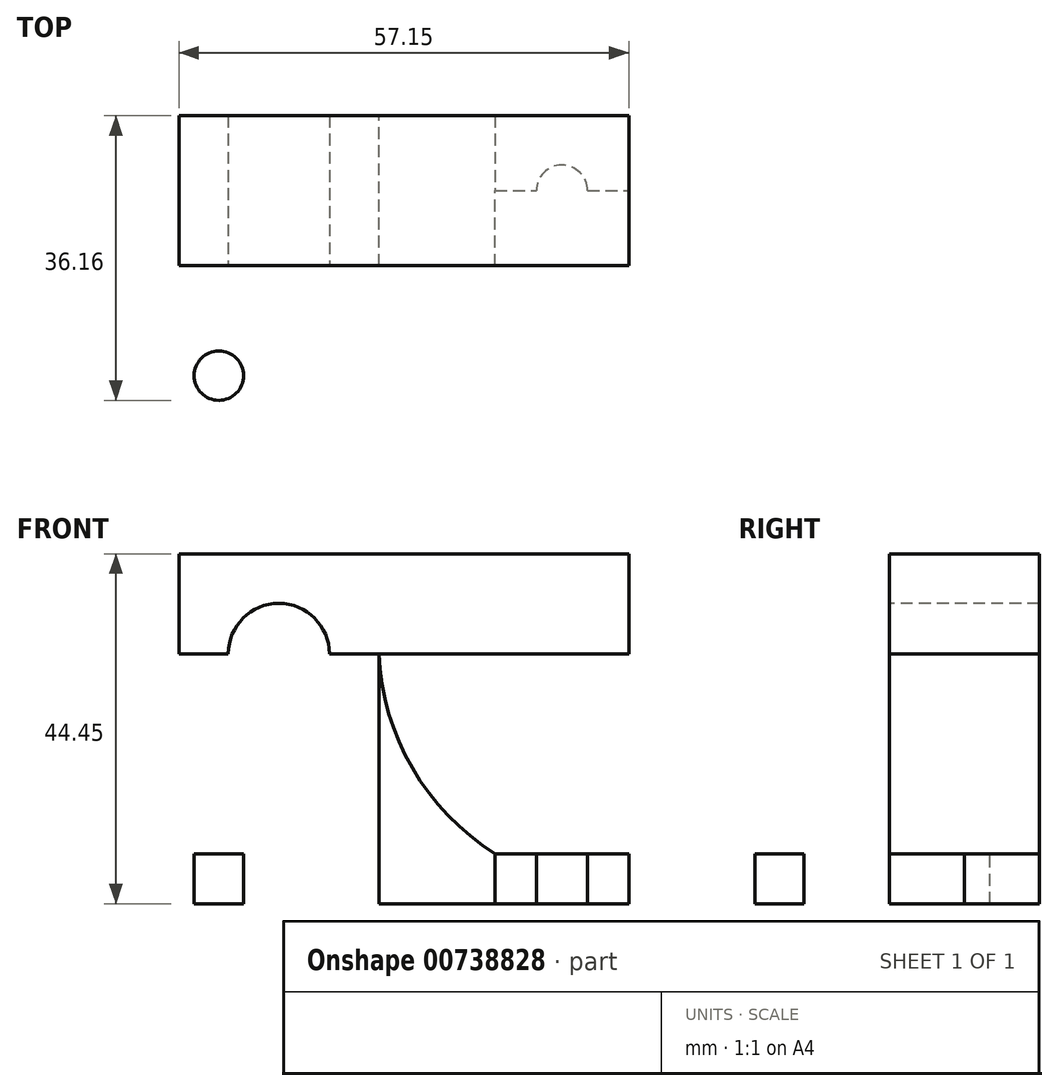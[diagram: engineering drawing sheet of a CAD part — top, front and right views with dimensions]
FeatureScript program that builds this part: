
annotation { "Feature Type Name" : "Feature", "Feature Type Description" : "" }
export const myFeature = defineFeature(function(context is Context, id is Id, definition is map)
    precondition{}
    {
        {
            var Q0;
            Q0=qCreatedBy(makeId("Front.planeOp"),FACE);
            var sketch = newSketch(context, id + "F0", { "sketchPlane" : qUnion([Q0])});
            skLineSegment(sketch, "E0", {"start": v(0, 0) * mm, "end": v(0, 44.45) * mm});
            skLineSegment(sketch, "E1", {"start": v(0, 44.45) * mm, "end": v(57.15, 44.45) * mm});
            skLineSegment(sketch, "E2", {"start": v(57.15, 44.45) * mm, "end": v(57.15, 0) * mm});
            skLineSegment(sketch, "E3", {"start": v(57.15, 0) * mm, "end": v(0, 0) * mm});
            skSolve(sketch);
        }
        {
            var Q0;
            Q0 = qSketchRegion(id + "F0", true);
            extrude(context, id + "F1", {"entities" : qUnion([Q0]), "depth" : 38.1 * mm, "offsetDistance" : 25.4 * mm});
        }
        {
            var Q0;
            Q0=makeQuery(id+"F1.opExtrude","CAP_FACE",FACE,{"disambiguationData":[OSD([sQuery(id+"F0.wireOp",EDGE,"E0"),sQuery(id+"F0.wireOp",EDGE,"E1"),sQuery(id+"F0.wireOp",EDGE,"E2"),sQuery(id+"F0.wireOp",EDGE,"E3")])],"isStart":false});
            var sketch = newSketch(context, id + "F2", { "sketchPlane" : qUnion([Q0])});
            skLineSegment(sketch, "E4", {"start": v(0, 6.35) * mm, "end": v(57.15, 6.35) * mm});
            skSolve(sketch);
        }
        {
            var Q0;
            {var subQ0=sQuery(id+"F2.wireOp",EDGE,"E4");Q0=makeQuery(id+"F2.imprint","IMPRINT",FACE,{"disambiguationData":[TD([[makeQuery(id+"F2.imprint","IMPRINT",EDGE,{"derivedFrom":subQ0}),1.0]])]});}
            extrude(context, id + "F3", {"entities" : qUnion([Q0]), "operationType" : NewBodyOperationType.REMOVE, "oppositeDirection" : true, "depth" : 19.05 * mm, "offsetDistance" : 25.4 * mm});
        }
        {
            var Q0;
            Q0=makeQuery(id+"F1.opExtrude","CAP_EDGE",EDGE,{"disambiguationData":[OSD([sQuery(id+"F0.wireOp",EDGE,"E0")])],"isStart":false});
            var Q1;
            Q1=makeQuery(id+"F1.opExtrude","CAP_EDGE",EDGE,{"disambiguationData":[OSD([sQuery(id+"F0.wireOp",EDGE,"E2")])],"isStart":false});
            fillet(context, id + "F4", {"entities" : qUnion([Q0, Q1]), "radius" : 5.08 * mm, "tangentPropagation" : true, "allowEdgeOverflow" : false});
        }
        {
            var Q0;
            Q0=makeQuery(id+"F3.boolean.opBoolean","COPY",FACE,{"derivedFrom":makeQuery(id+"F3.opExtrude","CAP_FACE",FACE,{"disambiguationData":[OSD([sQuery(id+"F0.wireOp",EDGE,"E0"),sQuery(id+"F0.wireOp",EDGE,"E1"),sQuery(id+"F0.wireOp",EDGE,"E2"),sQuery(id+"F2.wireOp",EDGE,"E4")])],"isStart":false})});
            var sketch = newSketch(context, id + "F5", { "sketchPlane" : qUnion([Q0])});
            skLineSegment(sketch, "E5", {"start": v(12.7, 44.45) * mm, "end": v(12.7, 6.35) * mm});
            skLineSegment(sketch, "E6", {"start": v(0, 31.75) * mm, "end": v(57.15, 31.75) * mm});
            skCircle(sketch, "E7", {"center": v(12.7, 31.75) * mm, "radius": 6.42 * mm});
            skLineSegment(sketch, "E8", {"start": v(25.4, 44.45) * mm, "end": v(25.4, 6.35) * mm});
            skPoint(sketch, "E8.endSnap0", {"position": v(28.58, 6.35) * mm});
            skArc(sketch, "E9", {"start": v(25.4, 31.75) * mm, "mid": v(12.7, 43.9) * mm, "end": v(0, 31.75) * mm});
            skArc(sketch, "E10", {"start": v(25.4, 31.75) * mm, "mid": v(29.66, 17.24) * mm, "end": v(40.16, 6.35) * mm});
            skSolve(sketch);
        }
        {
            var Q0;
            {var subQ0=sQuery(id+"F5.wireOp",EDGE,"E7");var subQ1=sQuery(id+"F5.wireOp",EDGE,"E5");var subQ2=makeQuery(id+"F5.imprint","INTERSECT",VERTEX,{"disambiguationData":[OD(0.0)],"derivedFrom":[subQ1,subQ0]});Q0=makeQuery(id+"F5.imprint","IMPRINT",FACE,{"disambiguationData":[TD([[makeQuery(id+"F5.imprint","IMPRINT",EDGE,{"disambiguationData":[TD([[subQ2,-1.0]])],"derivedFrom":subQ1}),-1.0]])]});}
            var Q1;
            {var subQ0=sQuery(id+"F5.wireOp",EDGE,"E7");var subQ1=sQuery(id+"F5.wireOp",EDGE,"E5");var subQ2=makeQuery(id+"F5.imprint","INTERSECT",VERTEX,{"disambiguationData":[OD(0.0)],"derivedFrom":[subQ1,subQ0]});Q1=makeQuery(id+"F5.imprint","IMPRINT",FACE,{"disambiguationData":[TD([[makeQuery(id+"F5.imprint","IMPRINT",EDGE,{"disambiguationData":[TD([[subQ2,-1.0]])],"derivedFrom":subQ1}),1.0]])]});}
            var Q2;
            {var subQ0=sQuery(id+"F5.wireOp",EDGE,"E6");var subQ1=sQuery(id+"F5.wireOp",EDGE,"E5");var subQ2=makeQuery(id+"F5.imprint","INTERSECT",VERTEX,{"derivedFrom":[subQ1,subQ0]});Q2=makeQuery(id+"F5.imprint","IMPRINT",FACE,{"disambiguationData":[TD([[makeQuery(id+"F5.imprint","IMPRINT",EDGE,{"disambiguationData":[TD([[subQ2,-1.0]])],"derivedFrom":subQ1}),-1.0]])]});}
            var Q3;
            {var subQ0=sQuery(id+"F5.wireOp",EDGE,"E6");var subQ1=sQuery(id+"F5.wireOp",EDGE,"E5");var subQ2=makeQuery(id+"F5.imprint","INTERSECT",VERTEX,{"derivedFrom":[subQ1,subQ0]});Q3=makeQuery(id+"F5.imprint","IMPRINT",FACE,{"disambiguationData":[TD([[makeQuery(id+"F5.imprint","IMPRINT",EDGE,{"disambiguationData":[TD([[subQ2,-1.0]])],"derivedFrom":subQ1}),1.0]])]});}
            var Q4;
            {var subQ0=sQuery(id+"F5.wireOp",EDGE,"E5");var subQ1=makeQuery(id+"F3.boolean.opBoolean","COPY",EDGE,{"derivedFrom":makeQuery(id+"F3.opExtrude","CAP_EDGE",EDGE,{"disambiguationData":[OSD([sQuery(id+"F0.wireOp",EDGE,"E1")])],"isStart":false})});var subQ2=makeQuery(id+"F5.imprint","INTERSECT",VERTEX,{"derivedFrom":[subQ1,subQ0]});Q4=makeQuery(id+"F5.imprint","IMPRINT",FACE,{"disambiguationData":[TD([[makeQuery(id+"F5.imprint","IMPRINT",EDGE,{"disambiguationData":[TD([[subQ2,-1.0]])],"derivedFrom":subQ0}),-1.0]])]});}
            var Q5;
            {var subQ0=sQuery(id+"F5.wireOp",EDGE,"E5");var subQ1=makeQuery(id+"F3.boolean.opBoolean","COPY",EDGE,{"derivedFrom":makeQuery(id+"F3.opExtrude","CAP_EDGE",EDGE,{"disambiguationData":[OSD([sQuery(id+"F0.wireOp",EDGE,"E1")])],"isStart":false})});var subQ2=makeQuery(id+"F5.imprint","INTERSECT",VERTEX,{"derivedFrom":[subQ1,subQ0]});Q5=makeQuery(id+"F5.imprint","IMPRINT",FACE,{"disambiguationData":[TD([[makeQuery(id+"F5.imprint","IMPRINT",EDGE,{"disambiguationData":[TD([[subQ2,-1.0]])],"derivedFrom":subQ0}),1.0]])]});}
            var Q6;
            {var subQ3=sQuery(id+"F5.wireOp",EDGE,"E10");Q6=makeQuery(id+"F5.imprint","IMPRINT",FACE,{"disambiguationData":[TD([[makeQuery(id+"F5.imprint","IMPRINT",EDGE,{"derivedFrom":subQ3}),1.0]])]});}
            var Q7;
            {var subQ1=makeQuery(id+"F3.boolean.opBoolean","COPY",EDGE,{"derivedFrom":makeQuery(id+"F3.opExtrude","CAP_EDGE",EDGE,{"disambiguationData":[OSD([sQuery(id+"F0.wireOp",EDGE,"E2")])],"isStart":false})});var subQ5=makeQuery(id+"F3.boolean.opBoolean","COPY",EDGE,{"derivedFrom":makeQuery(id+"F3.opExtrude","CAP_EDGE",EDGE,{"disambiguationData":[OSD([sQuery(id+"F0.wireOp",EDGE,"E1")])],"isStart":false})});var subQ7=makeQuery(id+"F5.imprint","INTERSECT",VERTEX,{"derivedFrom":[subQ5,subQ1]});Q7=makeQuery(id+"F5.imprint","IMPRINT",FACE,{"disambiguationData":[TD([[makeQuery(id+"F5.imprint","IMPRINT",EDGE,{"disambiguationData":[TD([[subQ7,1.0]])],"derivedFrom":subQ5}),-1.0]])]});}
            extrude(context, id + "F6", {"entities" : qUnion([Q0, Q1, Q2, Q3, Q4, Q5, Q6, Q7]), "operationType" : NewBodyOperationType.REMOVE, "endBound" : BoundingType.THROUGH_ALL, "oppositeDirection" : true, "depth" : 25.4 * mm, "offsetDistance" : 25.4 * mm});
        }
        {
            var Q0;
            {var subQ0=sQuery(id+"F2.wireOp",EDGE,"E4");Q0=makeQuery(id+"F6.boolean.opBoolean","MERGE",FACE,{"derivedFrom":[makeQuery(id+"F3.boolean.opBoolean","COPY",FACE,{"derivedFrom":makeQuery(id+"F3.opExtrude","SWEPT_FACE",FACE,{"disambiguationData":[OSD([subQ0])]})}),makeQuery(id+"F6.opExtrude","SWEPT_FACE",FACE,{"disambiguationData":[OSD([subQ0])]})]});}
            var sketch = newSketch(context, id + "F7", { "sketchPlane" : qUnion([Q0])});
            skLineSegment(sketch, "E11", {"start": v(40.16, -9.53) * mm, "end": v(57.15, -9.53) * mm});
            skCircle(sketch, "E12", {"center": v(48.66, -9.53) * mm, "radius": 3.25 * mm});
            skLineSegment(sketch, "E13", {"start": v(0, -33.02) * mm, "end": v(57.15, -33.02) * mm});
            skCircle(sketch, "E14", {"center": v(5.08, -33.02) * mm, "radius": 3.14 * mm});
            skCircle(sketch, "E15", {"center": v(48.66, -33.02) * mm, "radius": 3.18 * mm});
            skSolve(sketch);
        }
        {
            var Q0;
            {var subQ0=sQuery(id+"F7.wireOp",EDGE,"E14");var subQ1=sQuery(id+"F7.wireOp",EDGE,"E13");var subQ2=makeQuery(id+"F7.imprint","INTERSECT",VERTEX,{"disambiguationData":[OD(0.0)],"derivedFrom":[subQ1,subQ0]});Q0=makeQuery(id+"F7.imprint","IMPRINT",FACE,{"disambiguationData":[TD([[makeQuery(id+"F7.imprint","IMPRINT",EDGE,{"disambiguationData":[TD([[subQ2,-1.0]])],"derivedFrom":subQ1}),1.0]])]});}
            var Q1;
            {var subQ0=sQuery(id+"F7.wireOp",EDGE,"E14");var subQ1=sQuery(id+"F7.wireOp",EDGE,"E13");var subQ2=makeQuery(id+"F7.imprint","INTERSECT",VERTEX,{"disambiguationData":[OD(0.0)],"derivedFrom":[subQ1,subQ0]});Q1=makeQuery(id+"F7.imprint","IMPRINT",FACE,{"disambiguationData":[TD([[makeQuery(id+"F7.imprint","IMPRINT",EDGE,{"disambiguationData":[TD([[subQ2,-1.0]])],"derivedFrom":subQ1}),-1.0]])]});}
            var Q2;
            {var subQ0=sQuery(id+"F7.wireOp",EDGE,"E15");var subQ1=sQuery(id+"F7.wireOp",EDGE,"E13");var subQ2=makeQuery(id+"F7.imprint","INTERSECT",VERTEX,{"disambiguationData":[OD(0.0)],"derivedFrom":[subQ1,subQ0]});Q2=makeQuery(id+"F7.imprint","IMPRINT",FACE,{"disambiguationData":[TD([[makeQuery(id+"F7.imprint","IMPRINT",EDGE,{"disambiguationData":[TD([[subQ2,-1.0]])],"derivedFrom":subQ1}),1.0]])]});}
            var Q3;
            {var subQ0=sQuery(id+"F7.wireOp",EDGE,"E15");var subQ1=sQuery(id+"F7.wireOp",EDGE,"E13");var subQ2=makeQuery(id+"F7.imprint","INTERSECT",VERTEX,{"disambiguationData":[OD(0.0)],"derivedFrom":[subQ1,subQ0]});Q3=makeQuery(id+"F7.imprint","IMPRINT",FACE,{"disambiguationData":[TD([[makeQuery(id+"F7.imprint","IMPRINT",EDGE,{"disambiguationData":[TD([[subQ2,-1.0]])],"derivedFrom":subQ1}),-1.0]])]});}
            var Q4;
            {var subQ0=sQuery(id+"F7.wireOp",EDGE,"E12");var subQ1=sQuery(id+"F7.wireOp",EDGE,"E11");var subQ2=makeQuery(id+"F7.imprint","INTERSECT",VERTEX,{"disambiguationData":[OD(0.0)],"derivedFrom":[subQ1,subQ0]});Q4=makeQuery(id+"F7.imprint","IMPRINT",FACE,{"disambiguationData":[TD([[makeQuery(id+"F7.imprint","IMPRINT",EDGE,{"disambiguationData":[TD([[subQ2,-1.0]])],"derivedFrom":subQ1}),1.0]])]});}
            var Q5;
            {var subQ0=sQuery(id+"F7.wireOp",EDGE,"E12");var subQ1=sQuery(id+"F7.wireOp",EDGE,"E11");var subQ2=makeQuery(id+"F7.imprint","INTERSECT",VERTEX,{"disambiguationData":[OD(0.0)],"derivedFrom":[subQ1,subQ0]});Q5=makeQuery(id+"F7.imprint","IMPRINT",FACE,{"disambiguationData":[TD([[makeQuery(id+"F7.imprint","IMPRINT",EDGE,{"disambiguationData":[TD([[subQ2,-1.0]])],"derivedFrom":subQ1}),-1.0]])]});}
            extrude(context, id + "F8", {"entities" : qUnion([Q0, Q1, Q2, Q3, Q4, Q5]), "operationType" : NewBodyOperationType.REMOVE, "endBound" : BoundingType.THROUGH_ALL, "oppositeDirection" : true, "depth" : 25.4 * mm, "offsetDistance" : 25.4 * mm});
        }
    });
